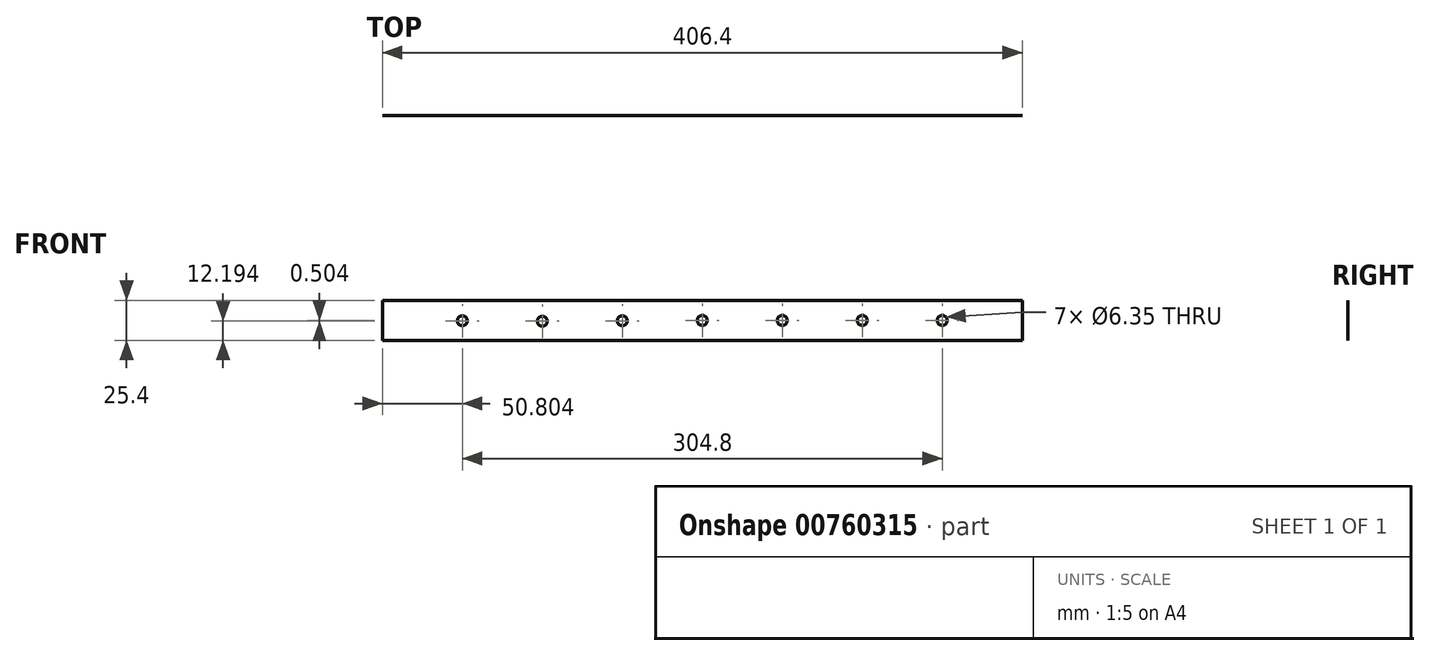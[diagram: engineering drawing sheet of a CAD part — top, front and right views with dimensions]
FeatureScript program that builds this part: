
annotation { "Feature Type Name" : "Feature", "Feature Type Description" : "" }
export const myFeature = defineFeature(function(context is Context, id is Id, definition is map)
    precondition{}
    {
        {
            var Q0;
            Q0=qCreatedBy(makeId("Front.planeOp"),FACE);
            var sketch = newSketch(context, id + "F0", { "sketchPlane" : qUnion([Q0])});
            skLineSegment(sketch, "E0.bottom", {"start": v(-66.35, -11.7) * mm, "end": v(340.05, -11.7) * mm});
            skLineSegment(sketch, "E0.top", {"start": v(-66.35, 13.7) * mm, "end": v(340.05, 13.7) * mm});
            skLineSegment(sketch, "E0.left", {"start": v(-66.35, -11.7) * mm, "end": v(-66.35, 13.7) * mm});
            skLineSegment(sketch, "E0.right", {"start": v(340.05, -11.7) * mm, "end": v(340.05, 13.7) * mm});
            skCircle(sketch, "E1", {"center": v(136.85, 1) * mm, "radius": 3.18 * mm});
            skCircle(sketch, "E2", {"center": v(238.45, 1) * mm, "radius": 3.18 * mm});
            skPoint(sketch, "E3.endSnap0", {"position": v(-66.35, 1) * mm});
            skCircle(sketch, "E4", {"center": v(35.25, 0.5) * mm, "radius": 3.18 * mm});
            skCircle(sketch, "E5", {"center": v(-15.55, 0.76) * mm, "radius": 3.18 * mm});
            skCircle(sketch, "E6", {"center": v(86.05, 0.76) * mm, "radius": 3.18 * mm});
            skCircle(sketch, "E7", {"center": v(187.65, 1) * mm, "radius": 3.18 * mm});
            skCircle(sketch, "E8", {"center": v(289.25, 1) * mm, "radius": 3.18 * mm});
            skSolve(sketch);
        }
        {
            var Q0;
            Q0=makeQuery(id+"F0.imprint","IMPRINT",FACE,{"disambiguationData":[TD([[makeQuery(id+"F0.imprint","IMPRINT",EDGE,{"derivedFrom":sQuery(id+"F0.wireOp",EDGE,"E0.bottom")}),1.0]])]});
            extrude(context, id + "F1", {"entities" : qUnion([Q0]), "depth" : 1 / 203.2 * mm, "offsetDistance" : 25.4 * mm});
        }
    });
